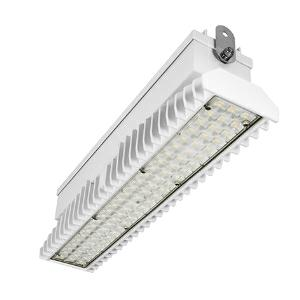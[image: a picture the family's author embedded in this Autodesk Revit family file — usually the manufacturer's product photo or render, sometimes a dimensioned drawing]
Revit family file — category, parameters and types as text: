
# Revit family: 3f_filippi_-_3f_lem_concentrato_3f_filippi_-_58887_a0811_-_3f_lem_1_led_50_cr_conc___vt_5583
name_source: partatom
category: Lighting Fixtures
units: mm (PartAtom-declared; Revit-internal decimal feet)

## family parameters
Cut with Voids When Loaded = No
Host = Face
Light Source = No
Part Type = Normal
Room Calculation Point = No
Round Connector Dimension = Use Diameter
Shared = No

## types (1)
- 3F Filippi - 3F LEM Concentrato (1 x LED, 7578 lm, 56 W, 4000 K)
    Apparent Load = 56 VA
    Approval mark = CE
    CIE Flux Codes = 83 96 99 100 100
    Color Rendering = 80
    Color Temperature = 4000 K
    Control Gear = Electronic ballast
    Default Elevation = 1800 mm
    Description = Industrial luminaire with high light output and high luminous efficiency designed with the most innovative technologies for environments with temperature up to 55°C.

ILLUMINOTECHNICAL
Luminous efficiency 100% (DLOR 99%, ULOR 1%).
Initial luminous flux of the luminaire 7578 lm.
Direct symmetric narrow distribution: the illuminated area has a elliptical shape.
Installation Interdistance Transv.D = 0.52 x hu - Long.D = 1.16 x hu.
Tabular UGR (CIE 117 - 4H-8H; S=0.25H; 70/50/20): RUG 20.2 - 24.
Beam angle: 31° - 73°.
Luminous efficacy 135 lm/W.
Lifetime (L93/B10): 30000 h. (tq+25°C)
Lifetime (L90/B10): 50000 h. (tq+25°C)
Lifetime (L85/B10): 80000 h. (tq+25°C)
Lifetime (L80/B10): 100000 h. (tq+25°C)
Lifetime (L85/B10): 50000 h. (tq+55°C)
Sudden decreased luminous flux after 50000 hours: 0% (C0).
Photobiological safety in compliance with IEC/TR 62778: RG0 risk exempt, (IEC 62471).
In compliance with IEC/EN 62722-2-1 - IEC/EN 62717 standards.

SOURCE
Mid-Power linear LED module 50W/840.
Energy efficiency class (UE 2019/2020 - UE 2019/2015): C.
CIE 13.3 Colour rendering index: CRI >80 (R9 <50%).
IES TM-30 Fidelity Index: Rf = 84 Rg = 95.
CCT nominal colour temperature 4000 K.
Colour initial tolerance (MacAdam): SDCM 3.

MECHANICAL
Passive modular heatsinks in die-casted aluminium, painted in white colour.
To optimize the thermal management of the LED module, the heatsinks are oversized and provided with self-cleaning of cooling fins.
Wiring body in aluminium and galvanised steel anchored solidly to the sinks and thermally separated.
3F Lens lenses with high luminous efficiency, transparent methacrylate (PMMA), fixed to the LED modules.
Fixing brackets in stainless steel.
Luminaire with limited surface temperature. - D - (EN 60598-2-24)
Dimensions: 542x115 mm, height 154 mm. Weight 6.397 kg.
IP65 protection degree.
Mechanical strength to impacts IK06 (1 joule).
Glow-wire test resistance 650°C.

ELECTRICAL
Halogen Free electronic wiring 230V-50/60Hz, power factor 0.95, THD <25%, constant output current, class I, 1 driver.
Power of the luminaire 56 W.
ENEC - CE.
SAFE FLICKER: PstLM=<1 and SVM=<0.4 (IEC TR 61547-1 and IEC TR 63158), to ensure a more comfortable and safe light.
Luminaire compliant with EN 60598-2-22 for power supply from a centralised emergency system CPSS (Central Power Supply System), not incorporated in the luminaire - high risk areas excluded. The default power and flux are 100% in AC and 100% in DC.
Ambient temperature from -30°C to +55°C.
Temperature class T6 max 85°C.
Quick connection via M20 3P connector with 9-13 mm tightening range.
Power unit positioned on a separate compartment by the LED module to ensure optimum temperatures of cabling components, to be inspectable and maintainable.
Relative humidity UR: <85%.

INSTALLATION
Ceiling / Suspended / Wall.
All accessories dedicated to this product are available on the Catalog and on our website www.3F-Filippi.com.

ACCESSORIES
A0811 - VT transparent glass, tempered, not flammable, with sealing gasket.
One required for each light module. The pack contains 10 pieces.

APPLICATIONS
In commercial environments, exhibition and industrial areas, stores, open areas.
Applications with high ambient temperature up to 55°C.
Environments in which it is necessary a total protection against falling fragments (eg environments with foodstuffs or machines with moving parts or with extreme temperature changes), use luminaires with polycarbonate lenses.

WARNING
Fixture not suitable for cold stores with an ambient temperature <0°C and/or relative humidity >85%.
Luminaire designed for disposal/recycling at end-of-life.
Replaceable (LED only) light source by a professional. Replaceable control gear by a professional.
    Height = 154 mm
    Lamp = 1 x LED
    Lamp Light Flux = 7578 lm
    Lamp Power = 56 W
    Lamp count = 1
    Length = 542 mm
    Lifetime = 50000 h
    Luminous efficacy = 135 lm/W
    Manufacturer = 3F Filippi
    ModVariant = No
    Model = 3F Filippi - 58887+A0811 - 3F LEM 1 LED 50 CR CONC + VT
    Mounting Place = Ceiling
    Mounting Type = Pendant
    Number of Poles = 1
    OnlyDefault = Yes
    Power Factor = 1
    Product Name = 3F Filippi - 3F LEM Concentrato
    Product group = pendant luminaire
    ProductGroupID = 9
    Protection Class = Protection class I
    Protection Degree = IP 65
    RLX_Detail_Level = 1
    RLX_Emergency_Light_Flux = 0 lm
    RLX_Emergency_Type = 0
    RLX_Emergency_Type_DB = No
    RlxData = <blob elided: 94553 chars, md5=d641b226>
    Socket = socket
    Standby Power = 0 W
    System Light Flux = 7578 lm
    System Power = 56 W
    Type Comments = Product without accessories
    Type Image = 3f_filippi_-_lem_1__a0811.jpg
    URL = http://relux.com
    VarID = ---
    Voltage = 0 V
    Weight = 0.00 kg
    Width = 115 mm

## geometry (parser evidence)
native form markers: Blend x4, Sweep x12
no freeform markers — native parametric forms only
